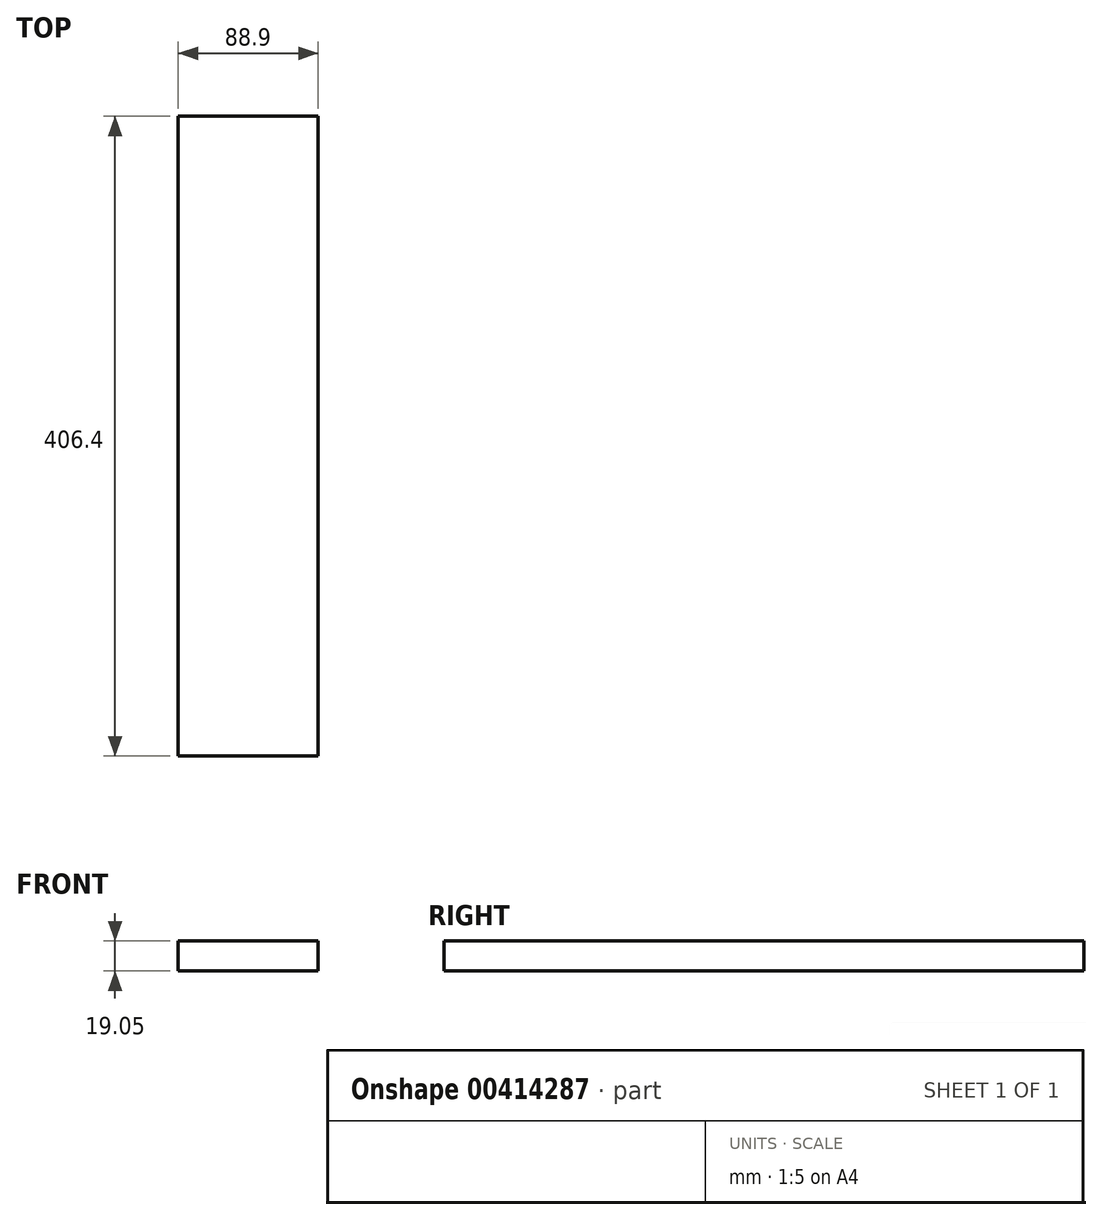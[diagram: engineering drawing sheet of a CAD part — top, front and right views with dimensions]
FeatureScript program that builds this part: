
annotation { "Feature Type Name" : "Feature", "Feature Type Description" : "" }
export const myFeature = defineFeature(function(context is Context, id is Id, definition is map)
    precondition{}
    {
        {
            var Q0;
            Q0=qCreatedBy(makeId("Front.planeOp"),FACE);
            var sketch = newSketch(context, id + "F0", { "sketchPlane" : qUnion([Q0])});
            skLineSegment(sketch, "E0.bottom", {"start": v(0, 0) * mm, "end": v(-88.9, 0) * mm});
            skLineSegment(sketch, "E0.top", {"start": v(0, 19.05) * mm, "end": v(-88.9, 19.05) * mm});
            skLineSegment(sketch, "E0.left", {"start": v(0, 0) * mm, "end": v(0, 19.05) * mm});
            skLineSegment(sketch, "E0.right", {"start": v(-88.9, 0) * mm, "end": v(-88.9, 19.05) * mm});
            skSolve(sketch);
        }
        {
            var Q0;
            Q0=qSketchRegion(id+"F0",true);
            extrude(context, id + "F1", {"entities" : qUnion([Q0]), "depth" : 406.4 * mm});
        }
    });
